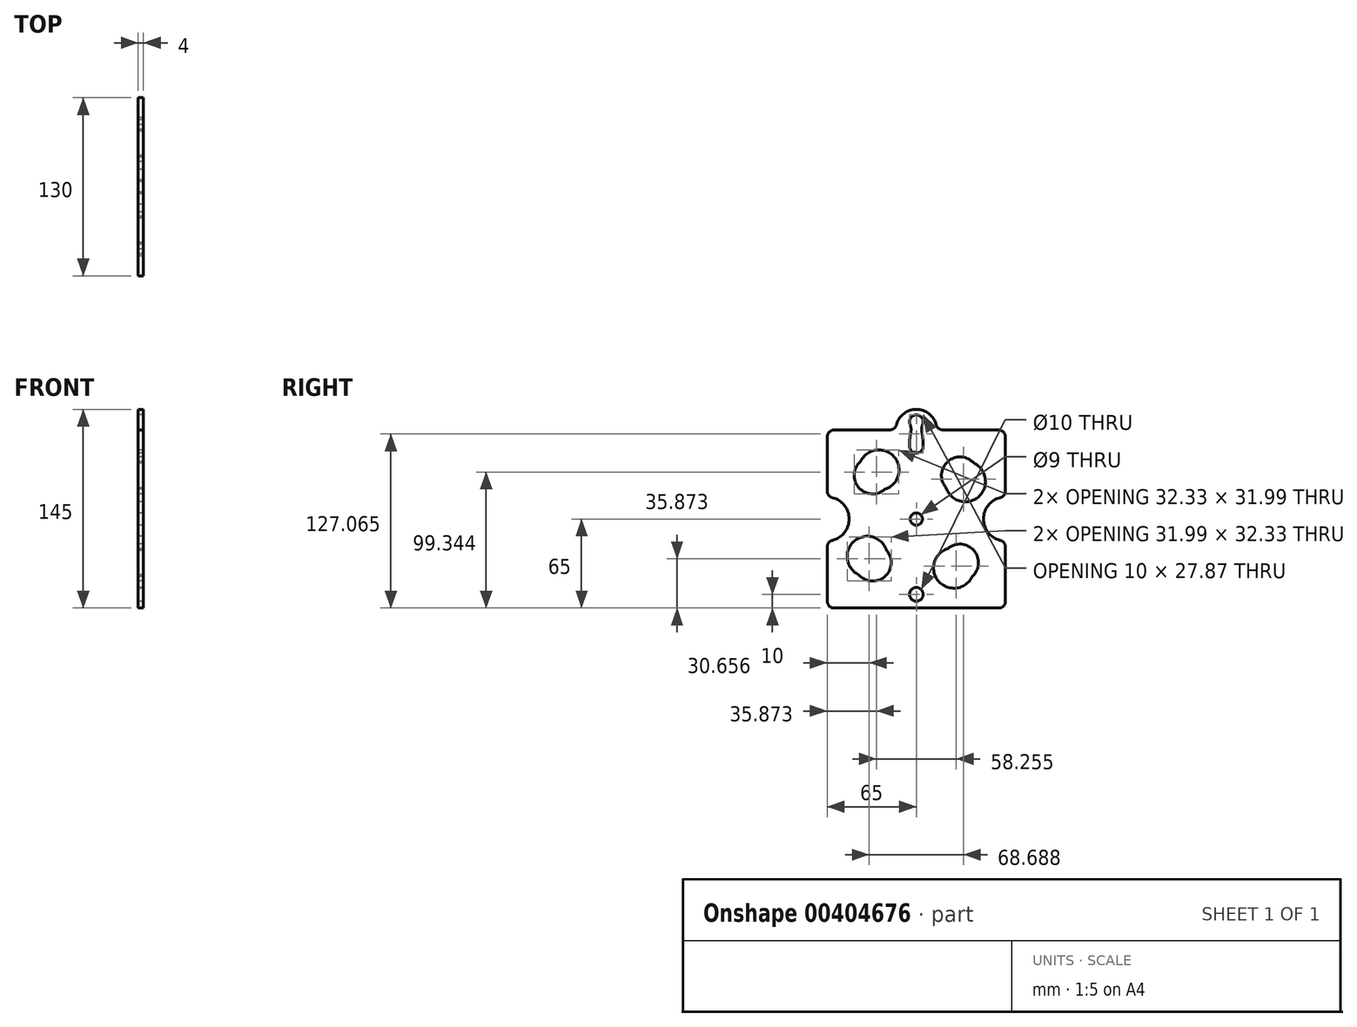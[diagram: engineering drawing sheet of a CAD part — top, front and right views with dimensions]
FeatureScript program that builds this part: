
annotation { "Feature Type Name" : "Feature", "Feature Type Description" : "" }
export const myFeature = defineFeature(function(context is Context, id is Id, definition is map)
    precondition{}
    {
        {
            var Q0;
            Q0=qCreatedBy(makeId("Right.planeOp"),FACE);
            var sketch = newSketch(context, id + "F0", { "sketchPlane" : qUnion([Q0])});
            skLineSegment(sketch, "E0.bottom", {"start": v(-60, 65) * mm, "end": v(-19.36, 65) * mm});
            skLineSegment(sketch, "E0.top", {"start": v(-60, -65) * mm, "end": v(60, -65) * mm});
            skLineSegment(sketch, "E0.right", {"start": v(65, 60) * mm, "end": v(65, 20.4) * mm});
            skArc(sketch, "E1", {"start": v(-40.71, 41.98) * mm, "mid": v(-41.98, 22.92) * mm, "end": v(-22.92, 21.66) * mm});
            skArc(sketch, "E2", {"start": v(-22.92, 21.66) * mm, "mid": v(-16.25, 45.45) * mm, "end": v(-40.71, 41.98) * mm});
            skArc(sketch, "E3.filletArc", {"start": v(-60, 65) * mm, "mid": v(-63.54, 63.54) * mm, "end": v(-65, 60) * mm});
            skPoint(sketch, "E4.visualSharp", {"position": v(65, 65) * mm});
            skArc(sketch, "E4.filletArc", {"start": v(65, 60) * mm, "mid": v(63.54, 63.54) * mm, "end": v(60, 65) * mm});
            skPoint(sketch, "E5.visualSharp", {"position": v(65, -65) * mm});
            skArc(sketch, "E5.filletArc", {"start": v(60, -65) * mm, "mid": v(63.54, -63.54) * mm, "end": v(65, -60) * mm});
            skLineSegment(sketch, "E6", {"start": v(-65, -60) * mm, "end": v(-65, -20.4) * mm});
            skLineSegment(sketch, "E7", {"start": v(-65, 0) * mm, "end": v(65, 0) * mm, "construction": true});
            skPoint(sketch, "E8.orphan", {"position": v(-65, -60) * mm});
            skPoint(sketch, "E9.visualSharp", {"position": v(-65, -65) * mm});
            skArc(sketch, "E9.filletArc", {"start": v(-65, -60) * mm, "mid": v(-63.54, -63.54) * mm, "end": v(-60, -65) * mm});
            skArc(sketch, "E10.1.0", {"start": v(-41.98, -40.71) * mm, "mid": v(-22.92, -41.98) * mm, "end": v(-21.66, -22.92) * mm});
            skArc(sketch, "E10.1.1", {"start": v(-21.66, -22.92) * mm, "mid": v(-45.45, -16.25) * mm, "end": v(-41.98, -40.71) * mm});
            skArc(sketch, "E10.2.0", {"start": v(40.71, -41.98) * mm, "mid": v(41.98, -22.92) * mm, "end": v(22.92, -21.66) * mm});
            skArc(sketch, "E10.2.1", {"start": v(22.92, -21.66) * mm, "mid": v(16.25, -45.45) * mm, "end": v(40.71, -41.98) * mm});
            skArc(sketch, "E10.3.0", {"start": v(41.98, 40.71) * mm, "mid": v(22.92, 41.98) * mm, "end": v(21.66, 22.92) * mm});
            skArc(sketch, "E10.3.1", {"start": v(21.66, 22.92) * mm, "mid": v(45.45, 16.25) * mm, "end": v(41.98, 40.71) * mm});
            skPoint(sketch, "E10.center", {"position": v(0, 0) * mm});
            skLineSegment(sketch, "E11.trimOffspring", {"start": v(19.36, 65) * mm, "end": v(60, 65) * mm});
            skCircle(sketch, "E12", {"center": v(0, 0) * mm, "radius": 4.5 * mm});
            skLineSegment(sketch, "E13", {"start": v(0, 0) * mm, "end": v(0, -55) * mm});
            skCircle(sketch, "E14", {"center": v(0, -55) * mm, "radius": 5 * mm});
            skArc(sketch, "E15", {"start": v(5, 71) * mm, "mid": v(0, 76) * mm, "end": v(-5, 71) * mm});
            skArc(sketch, "E16.trimOffspring", {"start": v(14.52, 68.75) * mm, "mid": v(0, 80) * mm, "end": v(-14.52, 68.75) * mm});
            skLineSegment(sketch, "E17", {"start": v(0, 71) * mm, "end": v(0, -65) * mm, "construction": true});
            skLineSegment(sketch, "E18", {"start": v(-31.82, 31.82) * mm, "end": v(0, 0) * mm, "construction": true});
            skArc(sketch, "E19", {"start": v(-5, 71) * mm, "mid": v(-4.9, 69.97) * mm, "end": v(-4.58, 68.99) * mm});
            skArc(sketch, "E20", {"start": v(-4.58, 68.99) * mm, "mid": v(-3.86, 66.29) * mm, "end": v(-4, 63.5) * mm});
            skArc(sketch, "E21", {"start": v(-4, 63.5) * mm, "mid": v(-4.79, 58.3) * mm, "end": v(-5, 53.06) * mm});
            skArc(sketch, "E22.MirrorCS", {"start": v(5, 71) * mm, "mid": v(4.9, 69.97) * mm, "end": v(4.58, 68.99) * mm});
            skArc(sketch, "E23.MirrorCS", {"start": v(4.58, 68.99) * mm, "mid": v(3.86, 66.29) * mm, "end": v(4, 63.5) * mm});
            skArc(sketch, "E24.MirrorCS", {"start": v(4, 63.5) * mm, "mid": v(4.79, 58.3) * mm, "end": v(5, 53.06) * mm});
            skArc(sketch, "E25", {"start": v(-5, 53.06) * mm, "mid": v(0, 48.13) * mm, "end": v(5, 53.06) * mm});
            skArc(sketch, "E26", {"start": v(-61.2, -15.54) * mm, "mid": v(-49, 0) * mm, "end": v(-61.2, 15.54) * mm});
            skLineSegment(sketch, "E27.trimOffspring", {"start": v(-65, 20.4) * mm, "end": v(-65, 60) * mm});
            skPoint(sketch, "E28.visualSharp", {"position": v(-65, 16) * mm});
            skArc(sketch, "E28.filletArc", {"start": v(-65, 20.4) * mm, "mid": v(-63.93, 17.31) * mm, "end": v(-61.2, 15.54) * mm});
            skPoint(sketch, "E29.visualSharp", {"position": v(-65, -16) * mm});
            skArc(sketch, "E29.filletArc", {"start": v(-61.2, -15.54) * mm, "mid": v(-63.93, -17.31) * mm, "end": v(-65, -20.4) * mm});
            skArc(sketch, "E30.MirrorCS", {"start": v(65, 20.4) * mm, "mid": v(63.93, 17.31) * mm, "end": v(61.2, 15.54) * mm});
            skArc(sketch, "E31.MirrorCS", {"start": v(61.2, -15.54) * mm, "mid": v(49, 0) * mm, "end": v(61.2, 15.54) * mm});
            skArc(sketch, "E32.MirrorCS", {"start": v(61.2, -15.54) * mm, "mid": v(63.93, -17.31) * mm, "end": v(65, -20.4) * mm});
            skLineSegment(sketch, "E33.trimOffspring", {"start": v(65, -20.4) * mm, "end": v(65, -60) * mm});
            skPoint(sketch, "E34.visualSharp", {"position": v(-15, 65) * mm});
            skArc(sketch, "E34.filletArc", {"start": v(-19.36, 65) * mm, "mid": v(-16.3, 66.05) * mm, "end": v(-14.52, 68.75) * mm});
            skPoint(sketch, "E35.visualSharp", {"position": v(15, 65) * mm});
            skArc(sketch, "E35.filletArc", {"start": v(14.52, 68.75) * mm, "mid": v(16.3, 66.05) * mm, "end": v(19.36, 65) * mm});
            skSolve(sketch);
        }
        {
            var Q0;
            Q0=makeQuery(id+"F0.imprint","IMPRINT",FACE,{"disambiguationData":[TD([[makeQuery(id+"F0.imprint","IMPRINT",EDGE,{"derivedFrom":sQuery(id+"F0.wireOp",EDGE,"E0.bottom")}),-1.0]])]});
            extrude(context, id + "F1", {"entities" : qUnion([Q0]), "depth" : 4 * mm});
        }
    });
